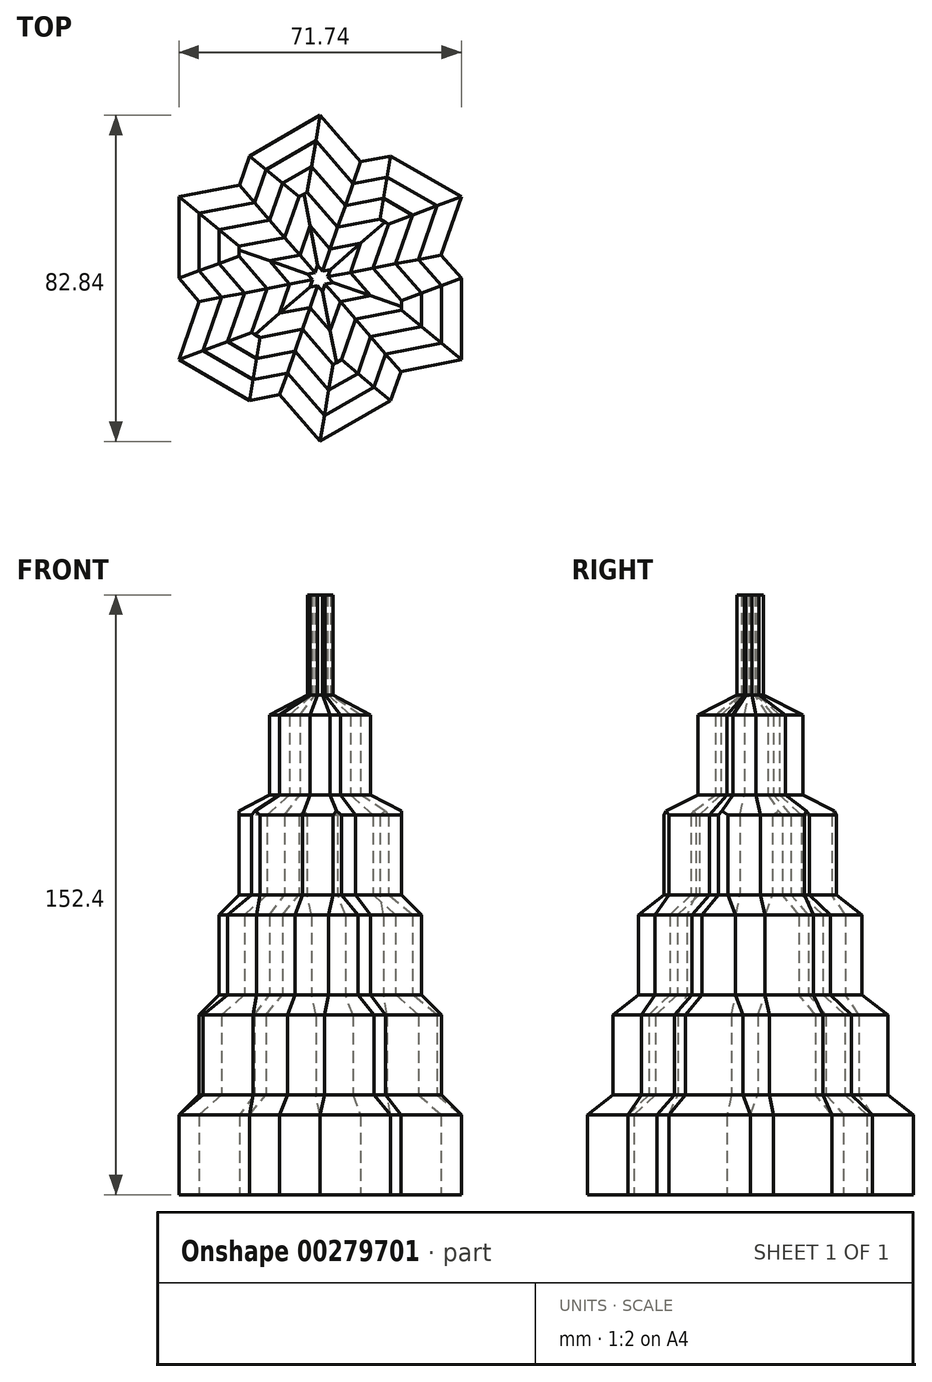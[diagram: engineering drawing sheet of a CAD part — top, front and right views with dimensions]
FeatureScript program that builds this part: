
annotation { "Feature Type Name" : "Feature", "Feature Type Description" : "" }
export const myFeature = defineFeature(function(context is Context, id is Id, definition is map)
    precondition{}
    {
        {
            var Q0;
            Q0=qCreatedBy(makeId("Top.planeOp"),FACE);
            var sketch = newSketch(context, id + "F0", { "sketchPlane" : qUnion([Q0])});
            skCircle(sketch, "E0.cCircle", {"center": v(0, 0) * mm, "radius": 35.87 * mm, "construction": true});
            skLineSegment(sketch, "E0.0", {"start": v(35.87, 20.7) * mm, "end": v(35.87, -20.7) * mm});
            skLineSegment(sketch, "E0.1", {"start": v(35.87, -20.7) * mm, "end": v(0, -41.42) * mm});
            skLineSegment(sketch, "E0.2", {"start": v(0, -41.42) * mm, "end": v(-35.87, -20.7) * mm});
            skLineSegment(sketch, "E0.3", {"start": v(-35.87, -20.7) * mm, "end": v(-35.87, 20.7) * mm});
            skLineSegment(sketch, "E0.4", {"start": v(-35.87, 20.7) * mm, "end": v(0, 41.42) * mm});
            skLineSegment(sketch, "E0.5", {"start": v(0, 41.42) * mm, "end": v(35.87, 20.7) * mm});
            skPoint(sketch, "E0.0.midPoint", {"position": v(35.87, 0) * mm});
            skLineSegment(sketch, "E1", {"start": v(0, 41.42) * mm, "end": v(35.87, 0) * mm});
            skLineSegment(sketch, "E2", {"start": v(35.87, 20.7) * mm, "end": v(17.93, -31.06) * mm});
            skLineSegment(sketch, "E3", {"start": v(35.87, -20.7) * mm, "end": v(-17.93, -31.06) * mm});
            skLineSegment(sketch, "E4", {"start": v(0, -41.42) * mm, "end": v(-35.87, 0) * mm});
            skLineSegment(sketch, "E5", {"start": v(-35.87, -20.7) * mm, "end": v(-17.93, 31.06) * mm});
            skLineSegment(sketch, "E6", {"start": v(-35.87, 20.7) * mm, "end": v(17.93, 31.06) * mm});
            skSolve(sketch);
        }
        {
            var Q0;
            {var subQ1=sQuery(id+"F0.wireOp",EDGE,"E0.4");var subQ3=sQuery(id+"F0.wireOp",EDGE,"E5");var subQ4=makeQuery(id+"F0.imprint","INTERSECT",VERTEX,{"derivedFrom":[subQ1,subQ3]});Q0=makeQuery(id+"F0.imprint","IMPRINT",FACE,{"disambiguationData":[TD([[makeQuery(id+"F0.imprint","IMPRINT",EDGE,{"disambiguationData":[TD([[subQ4,1.0]])],"derivedFrom":subQ3}),-1.0]])]});}
            var Q1;
            {var subQ7=sQuery(id+"F0.wireOp",EDGE,"E1");var subQ9=sQuery(id+"F0.wireOp",EDGE,"E6");var subQ10=makeQuery(id+"F0.imprint","INTERSECT",VERTEX,{"derivedFrom":[subQ7,subQ9]});Q1=makeQuery(id+"F0.imprint","IMPRINT",FACE,{"disambiguationData":[TD([[makeQuery(id+"F0.imprint","IMPRINT",EDGE,{"disambiguationData":[TD([[subQ10,-1.0]])],"derivedFrom":subQ7}),-1.0]])]});}
            var Q2;
            {var subQ3=sQuery(id+"F0.wireOp",EDGE,"E6");var subQ5=sQuery(id+"F0.wireOp",EDGE,"E1");var subQ6=makeQuery(id+"F0.imprint","INTERSECT",VERTEX,{"derivedFrom":[subQ5,subQ3]});Q2=makeQuery(id+"F0.imprint","IMPRINT",FACE,{"disambiguationData":[TD([[makeQuery(id+"F0.imprint","IMPRINT",EDGE,{"disambiguationData":[TD([[subQ6,-1.0]])],"derivedFrom":subQ5}),1.0]])]});}
            var Q3;
            {var subQ1=sQuery(id+"F0.wireOp",EDGE,"E0.0");var subQ3=sQuery(id+"F0.wireOp",EDGE,"E1");var subQ4=makeQuery(id+"F0.imprint","INTERSECT",VERTEX,{"derivedFrom":[subQ1,subQ3]});Q3=makeQuery(id+"F0.imprint","IMPRINT",FACE,{"disambiguationData":[TD([[makeQuery(id+"F0.imprint","IMPRINT",EDGE,{"disambiguationData":[TD([[subQ4,1.0]])],"derivedFrom":subQ3}),-1.0]])]});}
            var Q4;
            {var subQ1=sQuery(id+"F0.wireOp",EDGE,"E0.1");var subQ3=sQuery(id+"F0.wireOp",EDGE,"E2");var subQ4=makeQuery(id+"F0.imprint","INTERSECT",VERTEX,{"derivedFrom":[subQ1,subQ3]});Q4=makeQuery(id+"F0.imprint","IMPRINT",FACE,{"disambiguationData":[TD([[makeQuery(id+"F0.imprint","IMPRINT",EDGE,{"disambiguationData":[TD([[subQ4,1.0]])],"derivedFrom":subQ3}),-1.0]])]});}
            var Q5;
            {var subQ1=sQuery(id+"F0.wireOp",EDGE,"E0.2");var subQ3=sQuery(id+"F0.wireOp",EDGE,"E3");var subQ4=makeQuery(id+"F0.imprint","INTERSECT",VERTEX,{"derivedFrom":[subQ1,subQ3]});Q5=makeQuery(id+"F0.imprint","IMPRINT",FACE,{"disambiguationData":[TD([[makeQuery(id+"F0.imprint","IMPRINT",EDGE,{"disambiguationData":[TD([[subQ4,1.0]])],"derivedFrom":subQ3}),-1.0]])]});}
            var Q6;
            {var subQ1=sQuery(id+"F0.wireOp",EDGE,"E0.3");var subQ3=sQuery(id+"F0.wireOp",EDGE,"E4");var subQ4=makeQuery(id+"F0.imprint","INTERSECT",VERTEX,{"derivedFrom":[subQ1,subQ3]});Q6=makeQuery(id+"F0.imprint","IMPRINT",FACE,{"disambiguationData":[TD([[makeQuery(id+"F0.imprint","IMPRINT",EDGE,{"disambiguationData":[TD([[subQ4,1.0]])],"derivedFrom":subQ3}),-1.0]])]});}
            extrude(context, id + "F1", {"entities" : qUnion([Q0, Q1, Q2, Q3, Q4, Q5, Q6]), "depth" : 25.4 * mm});
        }
        {
            var Q0;
            Q0=makeQuery(id+"F1.opExtrude","CAP_FACE",FACE,{"disambiguationData":[OSD([sQuery(id+"F0.wireOp",EDGE,"E0.0"),sQuery(id+"F0.wireOp",EDGE,"E0.1"),sQuery(id+"F0.wireOp",EDGE,"E0.2"),sQuery(id+"F0.wireOp",EDGE,"E0.3"),sQuery(id+"F0.wireOp",EDGE,"E0.4"),sQuery(id+"F0.wireOp",EDGE,"E0.5"),sQuery(id+"F0.wireOp",EDGE,"E1"),sQuery(id+"F0.wireOp",EDGE,"E2"),sQuery(id+"F0.wireOp",EDGE,"E3"),sQuery(id+"F0.wireOp",EDGE,"E4"),sQuery(id+"F0.wireOp",EDGE,"E5"),sQuery(id+"F0.wireOp",EDGE,"E6")])],"isStart":false});
            chamfer(context, id + "F2", {"entities" : qUnion([Q0]), "width" : 5.08 * mm, "tangentPropagation" : true});
        }
        {
            var Q0;
            Q0=makeQuery(id+"F1.opExtrude","CAP_FACE",FACE,{"disambiguationData":[OSD([sQuery(id+"F0.wireOp",EDGE,"E0.0"),sQuery(id+"F0.wireOp",EDGE,"E0.1"),sQuery(id+"F0.wireOp",EDGE,"E0.2"),sQuery(id+"F0.wireOp",EDGE,"E0.3"),sQuery(id+"F0.wireOp",EDGE,"E0.4"),sQuery(id+"F0.wireOp",EDGE,"E0.5"),sQuery(id+"F0.wireOp",EDGE,"E1"),sQuery(id+"F0.wireOp",EDGE,"E2"),sQuery(id+"F0.wireOp",EDGE,"E3"),sQuery(id+"F0.wireOp",EDGE,"E4"),sQuery(id+"F0.wireOp",EDGE,"E5"),sQuery(id+"F0.wireOp",EDGE,"E6")])],"isStart":false});
            extrude(context, id + "F3", {"entities" : qUnion([Q0]), "operationType" : NewBodyOperationType.ADD, "depth" : 25.4 * mm});
        }
        {
            var Q0;
            Q0=makeQuery(id+"F3.opExtrude","CAP_FACE",FACE,{"disambiguationData":[OSD([sQuery(id+"F0.wireOp",EDGE,"E0.0"),sQuery(id+"F0.wireOp",EDGE,"E0.1"),sQuery(id+"F0.wireOp",EDGE,"E0.2"),sQuery(id+"F0.wireOp",EDGE,"E0.3"),sQuery(id+"F0.wireOp",EDGE,"E0.4"),sQuery(id+"F0.wireOp",EDGE,"E0.5"),sQuery(id+"F0.wireOp",EDGE,"E1"),sQuery(id+"F0.wireOp",EDGE,"E2"),sQuery(id+"F0.wireOp",EDGE,"E3"),sQuery(id+"F0.wireOp",EDGE,"E4"),sQuery(id+"F0.wireOp",EDGE,"E5"),sQuery(id+"F0.wireOp",EDGE,"E6")])],"isStart":false});
            chamfer(context, id + "F4", {"entities" : qUnion([Q0]), "width" : 5.08 * mm, "tangentPropagation" : true});
        }
        {
            var Q0;
            Q0=makeQuery(id+"F3.opExtrude","CAP_FACE",FACE,{"disambiguationData":[OSD([sQuery(id+"F0.wireOp",EDGE,"E0.0"),sQuery(id+"F0.wireOp",EDGE,"E0.1"),sQuery(id+"F0.wireOp",EDGE,"E0.2"),sQuery(id+"F0.wireOp",EDGE,"E0.3"),sQuery(id+"F0.wireOp",EDGE,"E0.4"),sQuery(id+"F0.wireOp",EDGE,"E0.5"),sQuery(id+"F0.wireOp",EDGE,"E1"),sQuery(id+"F0.wireOp",EDGE,"E2"),sQuery(id+"F0.wireOp",EDGE,"E3"),sQuery(id+"F0.wireOp",EDGE,"E4"),sQuery(id+"F0.wireOp",EDGE,"E5"),sQuery(id+"F0.wireOp",EDGE,"E6")])],"isStart":false});
            extrude(context, id + "F5", {"entities" : qUnion([Q0]), "operationType" : NewBodyOperationType.ADD, "depth" : 25.4 * mm});
        }
        {
            var Q0;
            Q0=makeQuery(id+"F5.opExtrude","CAP_FACE",FACE,{"disambiguationData":[OSD([sQuery(id+"F0.wireOp",EDGE,"E0.0"),sQuery(id+"F0.wireOp",EDGE,"E0.1"),sQuery(id+"F0.wireOp",EDGE,"E0.2"),sQuery(id+"F0.wireOp",EDGE,"E0.3"),sQuery(id+"F0.wireOp",EDGE,"E0.4"),sQuery(id+"F0.wireOp",EDGE,"E0.5"),sQuery(id+"F0.wireOp",EDGE,"E1"),sQuery(id+"F0.wireOp",EDGE,"E2"),sQuery(id+"F0.wireOp",EDGE,"E3"),sQuery(id+"F0.wireOp",EDGE,"E4"),sQuery(id+"F0.wireOp",EDGE,"E5"),sQuery(id+"F0.wireOp",EDGE,"E6")])],"isStart":false});
            chamfer(context, id + "F6", {"entities" : qUnion([Q0]), "width" : 5.08 * mm, "tangentPropagation" : true});
        }
        {
            var Q0;
            Q0=makeQuery(id+"F5.opExtrude","CAP_FACE",FACE,{"disambiguationData":[OSD([sQuery(id+"F0.wireOp",EDGE,"E0.0"),sQuery(id+"F0.wireOp",EDGE,"E0.1"),sQuery(id+"F0.wireOp",EDGE,"E0.2"),sQuery(id+"F0.wireOp",EDGE,"E0.3"),sQuery(id+"F0.wireOp",EDGE,"E0.4"),sQuery(id+"F0.wireOp",EDGE,"E0.5"),sQuery(id+"F0.wireOp",EDGE,"E1"),sQuery(id+"F0.wireOp",EDGE,"E2"),sQuery(id+"F0.wireOp",EDGE,"E3"),sQuery(id+"F0.wireOp",EDGE,"E4"),sQuery(id+"F0.wireOp",EDGE,"E5"),sQuery(id+"F0.wireOp",EDGE,"E6")])],"isStart":false});
            extrude(context, id + "F7", {"entities" : qUnion([Q0]), "operationType" : NewBodyOperationType.ADD, "depth" : 25.4 * mm});
        }
        {
            var Q0;
            Q0=makeQuery(id+"F7.opExtrude","CAP_FACE",FACE,{"disambiguationData":[OSD([sQuery(id+"F0.wireOp",EDGE,"E0.0"),sQuery(id+"F0.wireOp",EDGE,"E0.1"),sQuery(id+"F0.wireOp",EDGE,"E0.2"),sQuery(id+"F0.wireOp",EDGE,"E0.3"),sQuery(id+"F0.wireOp",EDGE,"E0.4"),sQuery(id+"F0.wireOp",EDGE,"E0.5"),sQuery(id+"F0.wireOp",EDGE,"E1"),sQuery(id+"F0.wireOp",EDGE,"E2"),sQuery(id+"F0.wireOp",EDGE,"E3"),sQuery(id+"F0.wireOp",EDGE,"E4"),sQuery(id+"F0.wireOp",EDGE,"E5"),sQuery(id+"F0.wireOp",EDGE,"E6")])],"isStart":false});
            chamfer(context, id + "F8", {"entities" : qUnion([Q0]), "width" : 5.08 * mm, "tangentPropagation" : true});
        }
        {
            var Q0;
            Q0=makeQuery(id+"F7.opExtrude","CAP_FACE",FACE,{"disambiguationData":[OSD([sQuery(id+"F0.wireOp",EDGE,"E0.0"),sQuery(id+"F0.wireOp",EDGE,"E0.1"),sQuery(id+"F0.wireOp",EDGE,"E0.2"),sQuery(id+"F0.wireOp",EDGE,"E0.3"),sQuery(id+"F0.wireOp",EDGE,"E0.4"),sQuery(id+"F0.wireOp",EDGE,"E0.5"),sQuery(id+"F0.wireOp",EDGE,"E1"),sQuery(id+"F0.wireOp",EDGE,"E2"),sQuery(id+"F0.wireOp",EDGE,"E3"),sQuery(id+"F0.wireOp",EDGE,"E4"),sQuery(id+"F0.wireOp",EDGE,"E5"),sQuery(id+"F0.wireOp",EDGE,"E6")])],"isStart":false});
            extrude(context, id + "F9", {"entities" : qUnion([Q0]), "operationType" : NewBodyOperationType.ADD, "depth" : 25.4 * mm});
        }
        {
            var Q0;
            Q0=makeQuery(id+"F9.opExtrude","CAP_FACE",FACE,{"disambiguationData":[OSD([sQuery(id+"F0.wireOp",EDGE,"E0.0"),sQuery(id+"F0.wireOp",EDGE,"E0.1"),sQuery(id+"F0.wireOp",EDGE,"E0.2"),sQuery(id+"F0.wireOp",EDGE,"E0.3"),sQuery(id+"F0.wireOp",EDGE,"E0.4"),sQuery(id+"F0.wireOp",EDGE,"E0.5"),sQuery(id+"F0.wireOp",EDGE,"E1"),sQuery(id+"F0.wireOp",EDGE,"E2"),sQuery(id+"F0.wireOp",EDGE,"E3"),sQuery(id+"F0.wireOp",EDGE,"E4"),sQuery(id+"F0.wireOp",EDGE,"E5"),sQuery(id+"F0.wireOp",EDGE,"E6")])],"isStart":false});
            chamfer(context, id + "F10", {"entities" : qUnion([Q0]), "width" : 5.08 * mm, "tangentPropagation" : true});
        }
        {
            var Q0;
            Q0=makeQuery(id+"F9.opExtrude","CAP_FACE",FACE,{"disambiguationData":[OSD([sQuery(id+"F0.wireOp",EDGE,"E0.0"),sQuery(id+"F0.wireOp",EDGE,"E0.1"),sQuery(id+"F0.wireOp",EDGE,"E0.2"),sQuery(id+"F0.wireOp",EDGE,"E0.3"),sQuery(id+"F0.wireOp",EDGE,"E0.4"),sQuery(id+"F0.wireOp",EDGE,"E0.5"),sQuery(id+"F0.wireOp",EDGE,"E1"),sQuery(id+"F0.wireOp",EDGE,"E2"),sQuery(id+"F0.wireOp",EDGE,"E3"),sQuery(id+"F0.wireOp",EDGE,"E4"),sQuery(id+"F0.wireOp",EDGE,"E5"),sQuery(id+"F0.wireOp",EDGE,"E6")])],"isStart":false});
            extrude(context, id + "F11", {"entities" : qUnion([Q0]), "operationType" : NewBodyOperationType.ADD, "depth" : 25.4 * mm});
        }
    });
